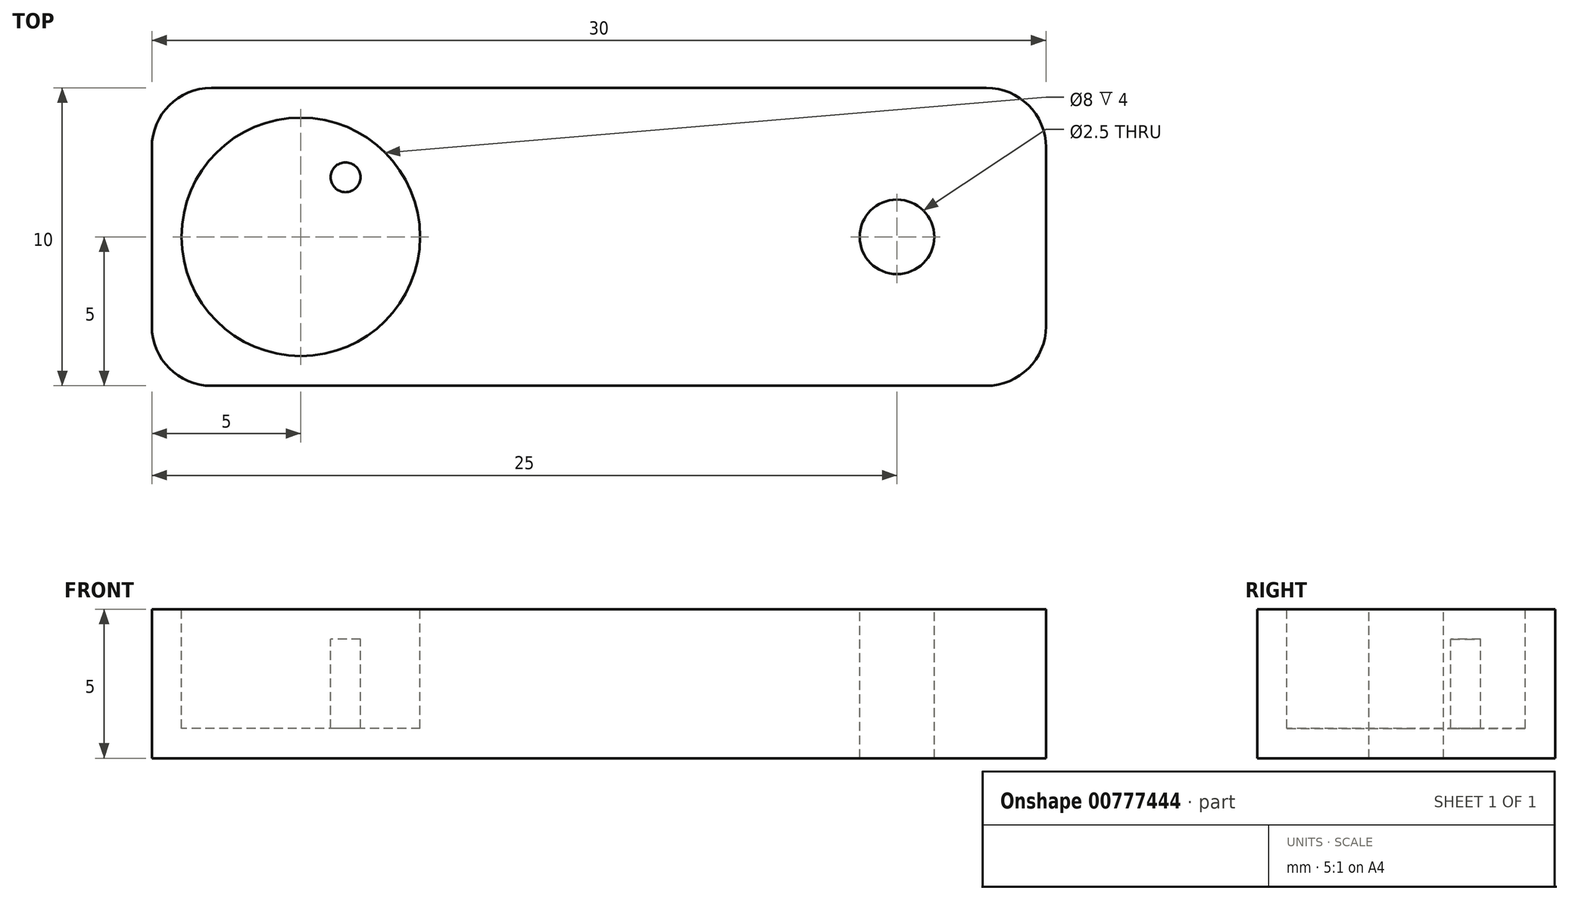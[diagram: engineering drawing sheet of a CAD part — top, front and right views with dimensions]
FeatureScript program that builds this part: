
annotation { "Feature Type Name" : "Feature", "Feature Type Description" : "" }
export const myFeature = defineFeature(function(context is Context, id is Id, definition is map)
    precondition{}
    {
        {
            var Q0;
            Q0=qCreatedBy(makeId("Top.planeOp"),FACE);
            var sketch = newSketch(context, id + "F0", { "sketchPlane" : qUnion([Q0])});
            skLineSegment(sketch, "E0.bottom", {"start": v(15, 5) * mm, "end": v(-15, 5) * mm});
            skLineSegment(sketch, "E0.top", {"start": v(15, -5) * mm, "end": v(-15, -5) * mm});
            skLineSegment(sketch, "E0.left", {"start": v(15, 5) * mm, "end": v(15, -5) * mm});
            skLineSegment(sketch, "E0.right", {"start": v(-15, 5) * mm, "end": v(-15, -5) * mm});
            skPoint(sketch, "E0.middle", {"position": v(0, 0) * mm});
            skSolve(sketch);
        }
        {
            var Q0;
            Q0=makeQuery(id+"F0.imprint","IMPRINT",FACE,{"disambiguationData":[TD([[makeQuery(id+"F0.imprint","IMPRINT",EDGE,{"derivedFrom":sQuery(id+"F0.wireOp",EDGE,"E0.bottom")}),1.0]])]});
            extrude(context, id + "F1", {"entities" : qUnion([Q0]), "endBound" : BoundingType.SYMMETRIC, "depth" : 5 * mm, "offsetDistance" : 25 * mm});
        }
        {
            var Q0;
            Q0=makeQuery(id+"F1.opExtrude","CAP_FACE",FACE,{"disambiguationData":[OSD([sQuery(id+"F0.wireOp",EDGE,"E0.bottom"),sQuery(id+"F0.wireOp",EDGE,"E0.top"),sQuery(id+"F0.wireOp",EDGE,"E0.left"),sQuery(id+"F0.wireOp",EDGE,"E0.right")])],"isStart":false});
            var sketch = newSketch(context, id + "F2", { "sketchPlane" : qUnion([Q0])});
            skCircle(sketch, "E1", {"center": v(-10, 0) * mm, "radius": 4 * mm});
            skSolve(sketch);
        }
        {
            var Q0;
            Q0=makeQuery(id+"F2.imprint","IMPRINT",FACE,{"disambiguationData":[TD([[makeQuery(id+"F2.imprint","IMPRINT",EDGE,{"derivedFrom":sQuery(id+"F2.wireOp",EDGE,"E1")}),1.0]])]});
            extrude(context, id + "F3", {"entities" : qUnion([Q0]), "operationType" : NewBodyOperationType.REMOVE, "oppositeDirection" : true, "depth" : 1 * mm, "offsetDistance" : 25 * mm});
        }
        {
            var Q0;
            Q0=makeQuery(id+"F3.boolean.opBoolean","COPY",FACE,{"derivedFrom":makeQuery(id+"F3.opExtrude","CAP_FACE",FACE,{"disambiguationData":[OSD([sQuery(id+"F2.wireOp",EDGE,"E1")])],"isStart":false})});
            var sketch = newSketch(context, id + "F4", { "sketchPlane" : qUnion([Q0])});
            skCircle(sketch, "E2", {"center": v(-11.5, 2) * mm, "radius": 0.5 * mm});
            skLineSegment(sketch, "E3", {"start": v(-10, 4) * mm, "end": v(-10, -4) * mm, "construction": true});
            skCircle(sketch, "E4.MirrorC", {"center": v(-8.5, 2) * mm, "radius": 0.5 * mm});
            skCircle(sketch, "E5", {"center": v(-10, -2) * mm, "radius": 0.5 * mm});
            skSolve(sketch);
        }
        {
            var Q0;
            Q0=makeQuery(id+"F4.imprint","IMPRINT",FACE,{"disambiguationData":[TD([[makeQuery(id+"F4.imprint","IMPRINT",EDGE,{"derivedFrom":sQuery(id+"F4.wireOp",EDGE,"E2")}),1.0]])]});
            var Q1;
            Q1=makeQuery(id+"F4.imprint","IMPRINT",FACE,{"disambiguationData":[TD([[makeQuery(id+"F4.imprint","IMPRINT",EDGE,{"derivedFrom":sQuery(id+"F4.wireOp",EDGE,"E4.MirrorC")}),-1.0]])]});
            var Q2;
            Q2=makeQuery(id+"F4.imprint","IMPRINT",FACE,{"disambiguationData":[TD([[makeQuery(id+"F4.imprint","IMPRINT",EDGE,{"derivedFrom":sQuery(id+"F4.wireOp",EDGE,"E5")}),1.0]])]});
            extrude(context, id + "F5", {"entities" : qUnion([Q0, Q1, Q2]), "operationType" : NewBodyOperationType.REMOVE, "oppositeDirection" : true, "depth" : 3 * mm, "offsetDistance" : 25 * mm});
        }
        {
            var Q0;
            Q0=makeQuery(id+"F1.opExtrude","CAP_FACE",FACE,{"disambiguationData":[OSD([sQuery(id+"F0.wireOp",EDGE,"E0.bottom"),sQuery(id+"F0.wireOp",EDGE,"E0.top"),sQuery(id+"F0.wireOp",EDGE,"E0.left"),sQuery(id+"F0.wireOp",EDGE,"E0.right")])],"isStart":false});
            var sketch = newSketch(context, id + "F6", { "sketchPlane" : qUnion([Q0])});
            skCircle(sketch, "E6", {"center": v(10, 0) * mm, "radius": 1.25 * mm});
            skSolve(sketch);
        }
        {
            var Q0;
            Q0=makeQuery(id+"F6.imprint","IMPRINT",FACE,{"disambiguationData":[TD([[makeQuery(id+"F6.imprint","IMPRINT",EDGE,{"derivedFrom":sQuery(id+"F6.wireOp",EDGE,"E6")}),1.0]])]});
            extrude(context, id + "F7", {"entities" : qUnion([Q0]), "operationType" : NewBodyOperationType.REMOVE, "endBound" : BoundingType.THROUGH_ALL, "oppositeDirection" : true, "depth" : 25 * mm, "offsetDistance" : 25 * mm});
        }
        {
            var Q0;
            Q0=makeQuery(id+"F1.opExtrude","SWEPT_EDGE",EDGE,{"disambiguationData":[OSD([sQuery(id+"F0.wireOp",EDGE,"E0.top"),sQuery(id+"F0.wireOp",EDGE,"E0.right")])]});
            var Q1;
            Q1=makeQuery(id+"F1.opExtrude","SWEPT_EDGE",EDGE,{"disambiguationData":[OSD([sQuery(id+"F0.wireOp",EDGE,"E0.bottom"),sQuery(id+"F0.wireOp",EDGE,"E0.right")])]});
            var Q2;
            Q2=makeQuery(id+"F1.opExtrude","SWEPT_EDGE",EDGE,{"disambiguationData":[OSD([sQuery(id+"F0.wireOp",EDGE,"E0.top"),sQuery(id+"F0.wireOp",EDGE,"E0.left")])]});
            var Q3;
            Q3=makeQuery(id+"F1.opExtrude","SWEPT_EDGE",EDGE,{"disambiguationData":[OSD([sQuery(id+"F0.wireOp",EDGE,"E0.bottom"),sQuery(id+"F0.wireOp",EDGE,"E0.left")])]});
            fillet(context, id + "F8", {"entities" : qUnion([Q0, Q1, Q2, Q3]), "radius" : 2 * mm, "tangentPropagation" : true, "allowEdgeOverflow" : false});
        }
    });
